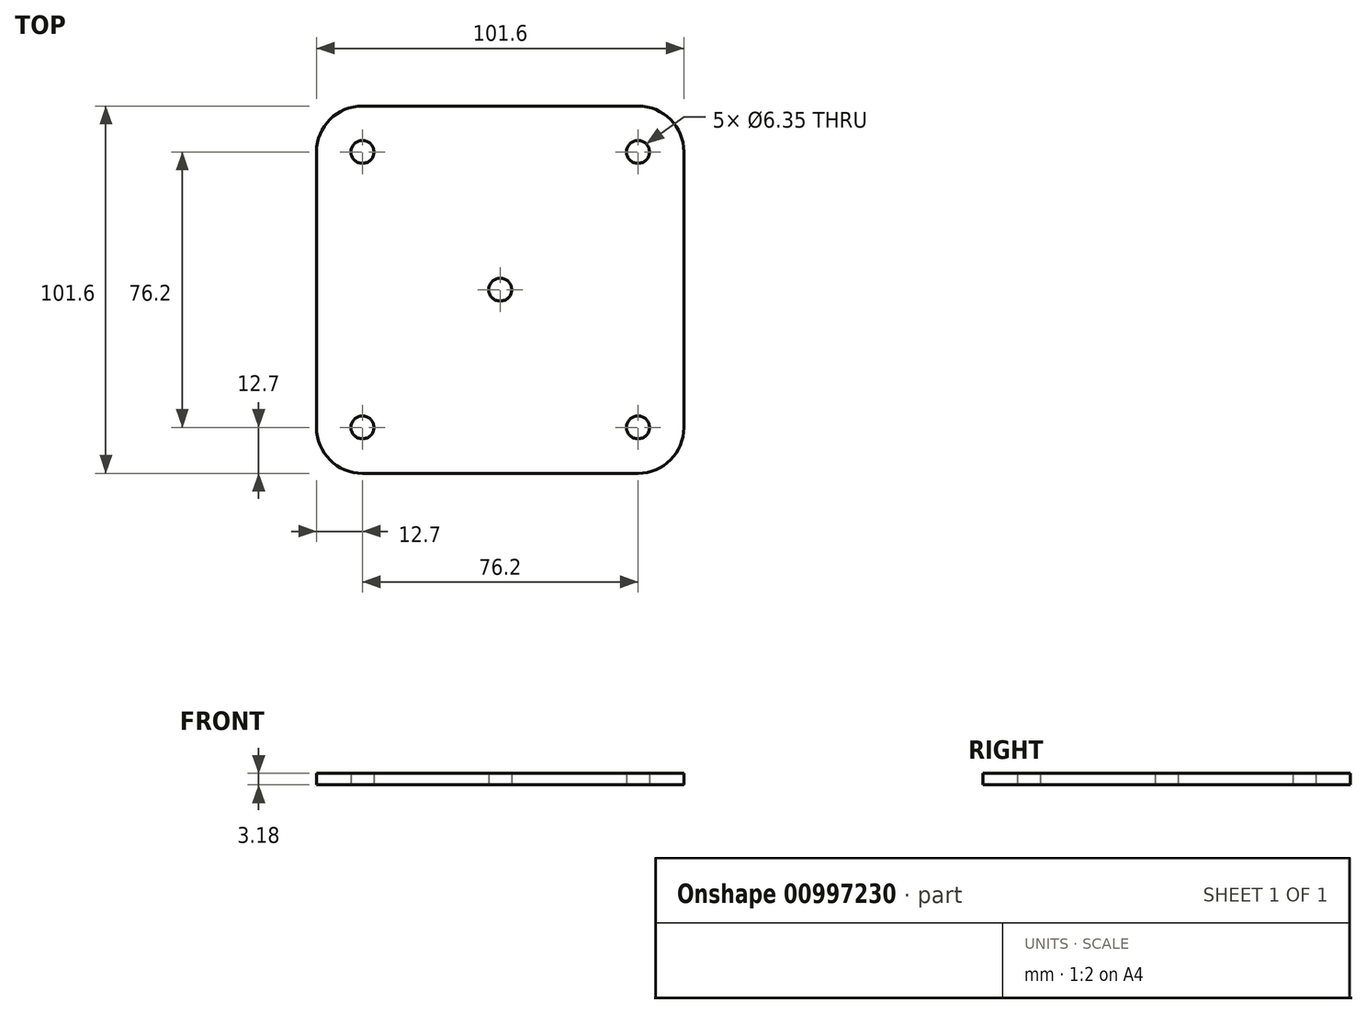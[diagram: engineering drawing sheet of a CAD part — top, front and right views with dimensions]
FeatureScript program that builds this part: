
annotation { "Feature Type Name" : "Feature", "Feature Type Description" : "" }
export const myFeature = defineFeature(function(context is Context, id is Id, definition is map)
    precondition{}
    {
        {
            var Q0;
            Q0=qCreatedBy(makeId("Top.planeOp"),FACE);
            var sketch = newSketch(context, id + "F0", { "sketchPlane" : qUnion([Q0])});
            skLineSegment(sketch, "E0.bottom", {"start": v(38.1, -50.8) * mm, "end": v(-38.1, -50.8) * mm});
            skLineSegment(sketch, "E0.top", {"start": v(38.1, 50.8) * mm, "end": v(-38.1, 50.8) * mm});
            skLineSegment(sketch, "E0.left", {"start": v(50.8, -38.1) * mm, "end": v(50.8, 38.1) * mm});
            skLineSegment(sketch, "E0.right", {"start": v(-50.8, -38.1) * mm, "end": v(-50.8, 38.1) * mm});
            skPoint(sketch, "E0.middle", {"position": v(0, 0) * mm});
            skPoint(sketch, "E1.visualSharp", {"position": v(-50.8, 50.8) * mm});
            skArc(sketch, "E1.filletArc", {"start": v(-38.1, 50.8) * mm, "mid": v(-47.08, 47.08) * mm, "end": v(-50.8, 38.1) * mm});
            skPoint(sketch, "E2.visualSharp", {"position": v(50.8, 50.8) * mm});
            skArc(sketch, "E2.filletArc", {"start": v(50.8, 38.1) * mm, "mid": v(47.08, 47.08) * mm, "end": v(38.1, 50.8) * mm});
            skPoint(sketch, "E3.visualSharp", {"position": v(-50.8, -50.8) * mm});
            skArc(sketch, "E3.filletArc", {"start": v(-50.8, -38.1) * mm, "mid": v(-47.08, -47.08) * mm, "end": v(-38.1, -50.8) * mm});
            skPoint(sketch, "E4.visualSharp", {"position": v(50.8, -50.8) * mm});
            skArc(sketch, "E4.filletArc", {"start": v(38.1, -50.8) * mm, "mid": v(47.08, -47.08) * mm, "end": v(50.8, -38.1) * mm});
            skCircle(sketch, "E5", {"center": v(-38.1, -38.1) * mm, "radius": 3.18 * mm});
            skCircle(sketch, "E6", {"center": v(38.1, -38.1) * mm, "radius": 3.18 * mm});
            skCircle(sketch, "E7", {"center": v(38.1, 38.1) * mm, "radius": 3.18 * mm});
            skCircle(sketch, "E8", {"center": v(-38.1, 38.1) * mm, "radius": 3.18 * mm});
            skCircle(sketch, "E9", {"center": v(0, 0) * mm, "radius": 3.18 * mm});
            skSolve(sketch);
        }
        {
            var Q0;
            Q0=makeQuery(id+"F0.imprint","IMPRINT",FACE,{"disambiguationData":[TD([[makeQuery(id+"F0.imprint","IMPRINT",EDGE,{"derivedFrom":sQuery(id+"F0.wireOp",EDGE,"E0.bottom")}),-1.0]])]});
            extrude(context, id + "F1", {"entities" : qUnion([Q0]), "endBound" : BoundingType.SYMMETRIC, "depth" : 3.17 * mm, "offsetDistance" : 25.4 * mm});
        }
    });
